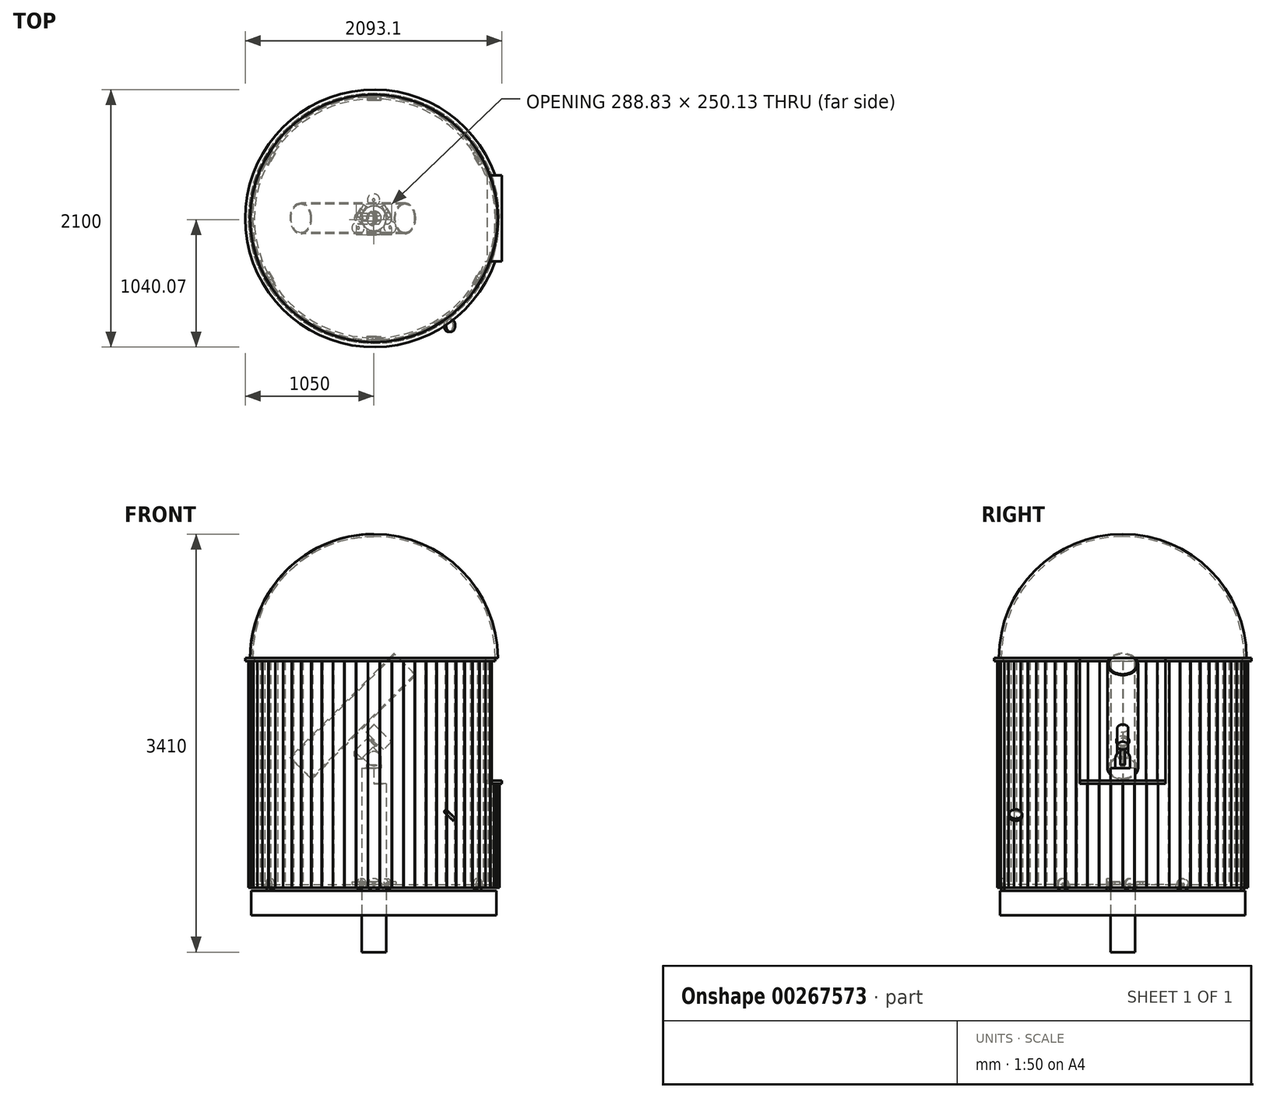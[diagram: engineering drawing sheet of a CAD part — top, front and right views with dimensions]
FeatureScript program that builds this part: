
annotation { "Feature Type Name" : "Feature", "Feature Type Description" : "" }
export const myFeature = defineFeature(function(context is Context, id is Id, definition is map)
    precondition{}
    {
        {
            assignVariable(context, id + "F0", {"name" : "Diameter", "anyValue" : 2000});
        }
        {
            assignVariable(context, id + "F1", {"name" : "Height", "anyValue" : 1850});
        }
        {
            assignVariable(context, id + "F2", {"name" : "TeleLength", "anyValue" : 1200});
        }
        {
            assignVariable(context, id + "F3", {"name" : "StandDia", "anyValue" : 200});
        }
        {
            var Q0;
            Q0=qCreatedBy(makeId("Top.planeOp"),FACE);
            var sketch = newSketch(context, id + "F4", { "sketchPlane" : qUnion([Q0])});
            skCircle(sketch, "E0", {"center": v(0, 0) * mm, "radius": 100 * mm});
            skSolve(sketch);
        }
        {
            var Q0;
            Q0 = qSketchRegion(id + "F4", true);
            extrude(context, id + "F5", {"entities" : qUnion([Q0]), "depth" : 1000 * mm, "hasSecondDirection" : true, "secondDirectionOppositeDirection" : true, "secondDirectionDepth" : 500 * mm});
        }
        {
            var Q0;
            Q0=qCreatedBy(makeId("Top.planeOp"),FACE);
            var sketch = newSketch(context, id + "F6", { "sketchPlane" : qUnion([Q0])});
            skCircle(sketch, "E1", {"center": v(0, 0) * mm, "radius": 1000 * mm});
            skSolve(sketch);
        }
        {
            var Q0;
            Q0 = qSketchRegion(id + "F6", true);
            extrude(context, id + "F7", {"entities" : qUnion([Q0]), "oppositeDirection" : true, "depth" : 200 * mm});
        }
        {
            var Q0;
            Q0=qCreatedBy(makeId("Front.planeOp"),FACE);
            cPlane(context, id + "F8", {"entities" : qUnion([Q0]), "cplaneType" : CPlaneType.OFFSET, "offset" : (getVariable(context, 'Diameter') / 2 - 10) * mm, "width" : 150 * mm, "height" : 150 * mm});
        }
        {
            var Q0;
            Q0=qCreatedBy(id+"F8.planeOp",FACE);
            var sketch = newSketch(context, id + "F9", { "sketchPlane" : qUnion([Q0])});
            skCircle(sketch, "E2", {"center": v(0, 50) * mm, "radius": 50 * mm});
            skCircle(sketch, "E3", {"center": v(0, 50) * mm, "radius": 10 * mm});
            skSolve(sketch);
        }
        {
            var Q0;
            Q0 = qSketchRegion(id + "F9", true);
            extrude(context, id + "F10", {"entities" : qUnion([Q0]), "oppositeDirection" : true, "depth" : 25 * mm});
        }
        {
            var Q0;
            Q0=makeQuery(id+"F10.opExtrude","SWEPT_BODY",BODY,{"disambiguationData":[OSD([sQuery(id+"F9.wireOp",EDGE,"E2"),sQuery(id+"F9.wireOp",EDGE,"E3")])]});
            var Q1;
            Q1=makeQuery(id+"F5.opExtrude","CAP_EDGE",EDGE,{"disambiguationData":[OSD([sQuery(id+"F4.wireOp",EDGE,"E0")])],"isStart":false});
            circularPattern(context, id + "F11", {"entities" : qUnion([Q0]), "axis" : qUnion([Q1]), "angle" : 360 * degree, "instanceCount" : 6, "equalSpace" : true});
        }
        {
            var Q0;
            Q0=makeQuery(id+"F10.opExtrude","SWEPT_BODY",BODY,{"disambiguationData":[OSD([sQuery(id+"F9.wireOp",EDGE,"E2"),sQuery(id+"F9.wireOp",EDGE,"E3")])]});
            transform(context, id + "F12", {"entities" : qUnion([Q0]), "transformType" : TransformType.TRANSLATION_3D, "dx" : 0 * mm, "dy" : (getVariable(context, 'Diameter') / 2 - getVariable(context, 'StandDia') / 2 - 40) * mm, "dz" : 0 * mm, "makeCopy" : true});
        }
        {
            var Q0;
            Q0=makeQuery(id+"F12.opPattern","COPY",BODY,{"derivedFrom":makeQuery(id+"F10.opExtrude","SWEPT_BODY",BODY,{"disambiguationData":[OSD([sQuery(id+"F9.wireOp",EDGE,"E2"),sQuery(id+"F9.wireOp",EDGE,"E3")])]}),"instanceName":"1"});
            var Q1;
            Q1=makeQuery(id+"F5.opExtrude","CAP_EDGE",EDGE,{"disambiguationData":[OSD([sQuery(id+"F4.wireOp",EDGE,"E0")])],"isStart":false});
            circularPattern(context, id + "F13", {"entities" : qUnion([Q0]), "axis" : qUnion([Q1]), "angle" : 360 * degree, "instanceCount" : 3, "equalSpace" : true});
        }
        {
            var Q0;
            Q0=makeQuery(id+"F7.opExtrude","CAP_FACE",FACE,{"disambiguationData":[OSD([sQuery(id+"F6.wireOp",EDGE,"E1")])],"isStart":true});
            cPlane(context, id + "F14", {"entities" : qUnion([Q0]), "cplaneType" : CPlaneType.OFFSET, "offset" : 25 * mm, "width" : 150 * mm, "height" : 150 * mm});
        }
        {
            var Q0;
            Q0=qCreatedBy(id+"F14.planeOp",FACE);
            var sketch = newSketch(context, id + "F15", { "sketchPlane" : qUnion([Q0])});
            skArc(sketch, "E4", {"start": v(55, -998.49) * mm, "mid": v(500, -866.03) * mm, "end": v(837.21, -546.87) * mm});
            skArc(sketch, "E5", {"start": v(52.92, -135) * mm, "mid": v(53.96, -134.59) * mm, "end": v(55, -134.16) * mm});
            skArc(sketch, "E6", {"start": v(55, -86.5) * mm, "mid": v(88.77, -51.25) * mm, "end": v(102.4, -4.38) * mm});
            skLineSegment(sketch, "E7", {"start": v(-55, -135) * mm, "end": v(55, -135) * mm});
            skLineSegment(sketch, "E8", {"start": v(-144.41, 19.87) * mm, "end": v(-89.41, 115.13) * mm});
            skLineSegment(sketch, "E9", {"start": v(144.41, 19.87) * mm, "end": v(89.41, 115.13) * mm});
            skLineSegment(sketch, "E10", {"start": v(55, -135) * mm, "end": v(55, -86.5) * mm});
            skLineSegment(sketch, "E11", {"start": v(-55, -135) * mm, "end": v(-55, -86.5) * mm});
            skLineSegment(sketch, "E12", {"start": v(-144.41, 19.87) * mm, "end": v(-102.4, -4.38) * mm});
            skLineSegment(sketch, "E13", {"start": v(-89.41, 115.13) * mm, "end": v(-47.4, 90.88) * mm});
            skLineSegment(sketch, "E14", {"start": v(102.4, -4.38) * mm, "end": v(144.41, 19.87) * mm});
            skLineSegment(sketch, "E15", {"start": v(47.4, 90.88) * mm, "end": v(89.41, 115.13) * mm});
            skLineSegment(sketch, "E16", {"start": v(-50, -130) * mm, "end": v(-50, -105) * mm, "construction": true});
            skLineSegment(sketch, "E17", {"start": v(50, -105) * mm, "end": v(50, -130) * mm, "construction": true});
            skLineSegment(sketch, "E18", {"start": v(137.58, 21.7) * mm, "end": v(115.93, 9.2) * mm, "construction": true});
            skLineSegment(sketch, "E19", {"start": v(65.93, 95.8) * mm, "end": v(87.58, 108.3) * mm, "construction": true});
            skLineSegment(sketch, "E20", {"start": v(-87.58, 108.3) * mm, "end": v(-65.93, 95.8) * mm, "construction": true});
            skLineSegment(sketch, "E21", {"start": v(-115.93, 9.2) * mm, "end": v(-137.58, 21.7) * mm, "construction": true});
            skPoint(sketch, "E22.orphan", {"position": v(159.25, -135) * mm});
            skArc(sketch, "E23.trimOffspring", {"start": v(143.69, 19.45) * mm, "mid": v(143.53, 20.56) * mm, "end": v(143.37, 21.67) * mm});
            skArc(sketch, "E24.trimOffspring", {"start": v(90.46, 113.33) * mm, "mid": v(89.58, 114.02) * mm, "end": v(88.69, 114.71) * mm});
            skPoint(sketch, "E25.orphan", {"position": v(159.25, 155.45) * mm});
            skArc(sketch, "E26.trimOffspring", {"start": v(-88.69, 114.71) * mm, "mid": v(-89.58, 114.02) * mm, "end": v(-90.46, 113.33) * mm});
            skArc(sketch, "E27.trimOffspring", {"start": v(47.4, 90.88) * mm, "mid": v(0, 102.5) * mm, "end": v(-47.4, 90.88) * mm});
            skArc(sketch, "E28.trimOffspring", {"start": v(-102.4, -4.38) * mm, "mid": v(-88.77, -51.25) * mm, "end": v(-55, -86.5) * mm});
            skArc(sketch, "E29.trimOffspring", {"start": v(-143.37, 21.67) * mm, "mid": v(-143.53, 20.56) * mm, "end": v(-143.69, 19.45) * mm});
            skArc(sketch, "E30.trimOffspring", {"start": v(-55, -134.16) * mm, "mid": v(-53.96, -134.59) * mm, "end": v(-52.92, -135) * mm});
            skLineSegment(sketch, "E31", {"start": v(-55, -998.49) * mm, "end": v(-55, -960) * mm});
            skLineSegment(sketch, "E32", {"start": v(-55, -960) * mm, "end": v(55, -960) * mm});
            skLineSegment(sketch, "E33", {"start": v(55, -998.49) * mm, "end": v(55, -960) * mm});
            skLineSegment(sketch, "E34", {"start": v(-50, -990) * mm, "end": v(-50, -965) * mm, "construction": true});
            skLineSegment(sketch, "E35", {"start": v(50, -965) * mm, "end": v(50, -990) * mm, "construction": true});
            skLineSegment(sketch, "E36.1.0", {"start": v(860.71, -439.2) * mm, "end": v(882.37, -451.7) * mm, "construction": true});
            skLineSegment(sketch, "E36.1.1", {"start": v(803.88, -527.63) * mm, "end": v(858.88, -432.37) * mm});
            skLineSegment(sketch, "E36.1.2", {"start": v(832.37, -538.3) * mm, "end": v(810.71, -525.8) * mm, "construction": true});
            skLineSegment(sketch, "E36.1.3", {"start": v(837.21, -546.87) * mm, "end": v(803.88, -527.63) * mm});
            skLineSegment(sketch, "E36.1.4", {"start": v(892.21, -451.61) * mm, "end": v(858.88, -432.37) * mm});
            skLineSegment(sketch, "E36.2.0", {"start": v(810.71, 525.8) * mm, "end": v(832.37, 538.3) * mm, "construction": true});
            skLineSegment(sketch, "E36.2.1", {"start": v(858.88, 432.37) * mm, "end": v(803.88, 527.63) * mm});
            skLineSegment(sketch, "E36.2.2", {"start": v(882.37, 451.7) * mm, "end": v(860.71, 439.2) * mm, "construction": true});
            skLineSegment(sketch, "E36.2.3", {"start": v(892.21, 451.61) * mm, "end": v(858.88, 432.37) * mm});
            skLineSegment(sketch, "E36.2.4", {"start": v(837.21, 546.87) * mm, "end": v(803.88, 527.63) * mm});
            skLineSegment(sketch, "E36.3.0", {"start": v(-50, 965) * mm, "end": v(-50, 990) * mm, "construction": true});
            skLineSegment(sketch, "E36.3.1", {"start": v(55, 960) * mm, "end": v(-55, 960) * mm});
            skLineSegment(sketch, "E36.3.2", {"start": v(50, 990) * mm, "end": v(50, 965) * mm, "construction": true});
            skLineSegment(sketch, "E36.3.3", {"start": v(55, 998.49) * mm, "end": v(55, 960) * mm});
            skLineSegment(sketch, "E36.3.4", {"start": v(-55, 998.49) * mm, "end": v(-55, 960) * mm});
            skLineSegment(sketch, "E36.4.0", {"start": v(-860.71, 439.2) * mm, "end": v(-882.37, 451.7) * mm, "construction": true});
            skLineSegment(sketch, "E36.4.1", {"start": v(-803.88, 527.63) * mm, "end": v(-858.88, 432.37) * mm});
            skLineSegment(sketch, "E36.4.2", {"start": v(-832.37, 538.3) * mm, "end": v(-810.71, 525.8) * mm, "construction": true});
            skLineSegment(sketch, "E36.4.3", {"start": v(-837.21, 546.87) * mm, "end": v(-803.88, 527.63) * mm});
            skLineSegment(sketch, "E36.4.4", {"start": v(-892.21, 451.61) * mm, "end": v(-858.88, 432.37) * mm});
            skLineSegment(sketch, "E36.5.0", {"start": v(-810.71, -525.8) * mm, "end": v(-832.37, -538.3) * mm, "construction": true});
            skLineSegment(sketch, "E36.5.1", {"start": v(-858.88, -432.37) * mm, "end": v(-803.88, -527.63) * mm});
            skLineSegment(sketch, "E36.5.2", {"start": v(-882.37, -451.7) * mm, "end": v(-860.71, -439.2) * mm, "construction": true});
            skLineSegment(sketch, "E36.5.3", {"start": v(-892.21, -451.61) * mm, "end": v(-858.88, -432.37) * mm});
            skLineSegment(sketch, "E36.5.4", {"start": v(-837.21, -546.87) * mm, "end": v(-803.88, -527.63) * mm});
            skArc(sketch, "E37.trimOffspring", {"start": v(-837.21, -546.87) * mm, "mid": v(-500, -866.03) * mm, "end": v(-55, -998.49) * mm});
            skArc(sketch, "E38.trimOffspring", {"start": v(-892.21, 451.61) * mm, "mid": v(-1000, 0) * mm, "end": v(-892.21, -451.61) * mm});
            skArc(sketch, "E39.trimOffspring", {"start": v(-55, 998.49) * mm, "mid": v(-500, 866.03) * mm, "end": v(-837.21, 546.87) * mm});
            skArc(sketch, "E40.trimOffspring", {"start": v(837.21, 546.87) * mm, "mid": v(500, 866.03) * mm, "end": v(55, 998.49) * mm});
            skArc(sketch, "E41.trimOffspring", {"start": v(892.21, -451.61) * mm, "mid": v(1000, 0) * mm, "end": v(892.21, 451.61) * mm});
            skSolve(sketch);
        }
        {
            var Q0;
            Q0 = qSketchRegion(id + "F15", true);
            extrude(context, id + "F16", {"entities" : qUnion([Q0]), "depth" : 25 * mm});
        }
        {
            var Q0;
            Q0=makeQuery(id+"F16.opExtrude","CAP_FACE",FACE,{"disambiguationData":[OSD([sQuery(id+"F15.wireOp",EDGE,"E4"),sQuery(id+"F15.wireOp",EDGE,"E6"),sQuery(id+"F15.wireOp",EDGE,"E7"),sQuery(id+"F15.wireOp",EDGE,"E8"),sQuery(id+"F15.wireOp",EDGE,"E9"),sQuery(id+"F15.wireOp",EDGE,"E10"),sQuery(id+"F15.wireOp",EDGE,"E11"),sQuery(id+"F15.wireOp",EDGE,"E12"),sQuery(id+"F15.wireOp",EDGE,"E13"),sQuery(id+"F15.wireOp",EDGE,"E14"),sQuery(id+"F15.wireOp",EDGE,"E15"),sQuery(id+"F15.wireOp",EDGE,"E27.trimOffspring"),sQuery(id+"F15.wireOp",EDGE,"E28.trimOffspring")])],"isStart":false});
            var sketch = newSketch(context, id + "F17", { "sketchPlane" : qUnion([Q0])});
            skCircle(sketch, "E42", {"center": v(131.23, -72.66) * mm, "radius": 50 * mm});
            skLineSegment(sketch, "E43", {"start": v(0, 0) * mm, "end": v(285.88, -158.3) * mm, "construction": true});
            skLineSegment(sketch, "E44", {"start": v(0, 0) * mm, "end": v(432.41, 7.74) * mm, "construction": true});
            skPoint(sketch, "E44.endSnap0", {"position": v(123.4, 7.74) * mm});
            skCircle(sketch, "E45", {"center": v(131.23, -72.66) * mm, "radius": 10 * mm});
            skSolve(sketch);
        }
        {
            var Q0;
            Q0 = qSketchRegion(id + "F17", true);
            extrude(context, id + "F18", {"entities" : qUnion([Q0]), "depth" : 25 * mm});
        }
        {
            var Q0;
            Q0=makeQuery(id+"F18.opExtrude","SWEPT_BODY",BODY,{"disambiguationData":[OSD([sQuery(id+"F17.wireOp",EDGE,"E42"),sQuery(id+"F17.wireOp",EDGE,"E45")])]});
            var Q1;
            Q1=makeQuery(id+"F5.opExtrude","CAP_EDGE",EDGE,{"disambiguationData":[OSD([sQuery(id+"F4.wireOp",EDGE,"E0")])],"isStart":false});
            circularPattern(context, id + "F19", {"entities" : qUnion([Q0]), "axis" : qUnion([Q1]), "angle" : 360 * degree, "instanceCount" : 3, "equalSpace" : true});
        }
        {
            var Q0;
            Q0=qCreatedBy(id+"F14.planeOp",FACE);
            var sketch = newSketch(context, id + "F20", { "sketchPlane" : qUnion([Q0])});
            skLineSegment(sketch, "E46.bottom", {"start": v(47.5, -1022) * mm, "end": v(-47.5, -1022) * mm});
            skLineSegment(sketch, "E46.top", {"start": v(47.5, -1000) * mm, "end": v(-47.5, -1000) * mm});
            skLineSegment(sketch, "E46.left", {"start": v(47.5, -1022) * mm, "end": v(47.5, -1000) * mm});
            skLineSegment(sketch, "E46.right", {"start": v(-47.5, -1022) * mm, "end": v(-47.5, -1000) * mm});
            skPoint(sketch, "E46.middle", {"position": v(0, -1011) * mm});
            skSolve(sketch);
        }
        {
            var Q0;
            Q0 = qSketchRegion(id + "F20", true);
            extrude(context, id + "F21", {"entities" : qUnion([Q0]), "depth" : (getVariable(context, 'Height')) * mm});
        }
        {
            var Q0;
            Q0=makeQuery(id+"F21.opExtrude","SWEPT_BODY",BODY,{"disambiguationData":[OSD([sQuery(id+"F20.wireOp",EDGE,"E46.bottom"),sQuery(id+"F20.wireOp",EDGE,"E46.top"),sQuery(id+"F20.wireOp",EDGE,"E46.left"),sQuery(id+"F20.wireOp",EDGE,"E46.right")])]});
            var Q1;
            Q1=makeQuery(id+"F5.opExtrude","CAP_EDGE",EDGE,{"disambiguationData":[OSD([sQuery(id+"F4.wireOp",EDGE,"E0")])],"isStart":false});
            circularPattern(context, id + "F22", {"entities" : qUnion([Q0]), "axis" : qUnion([Q1]), "angle" : 360 * degree, "instanceCount" : floor(getVariable(context, 'Diameter') * PI / 95), "equalSpace" : true});
        }
        {
            var Q0;
            Q0=qCreatedBy(makeId("Right.planeOp"),FACE);
            var sketch = newSketch(context, id + "F23", { "sketchPlane" : qUnion([Q0])});
            skLineSegment(sketch, "E47.bottom", {"start": v(350, 875) * mm, "end": v(-350, 875) * mm});
            skLineSegment(sketch, "E47.top", {"start": v(350, 2256.82) * mm, "end": v(-350, 2256.82) * mm});
            skLineSegment(sketch, "E47.left", {"start": v(350, 875) * mm, "end": v(350, 2256.82) * mm});
            skLineSegment(sketch, "E47.right", {"start": v(-350, 875) * mm, "end": v(-350, 2256.82) * mm});
            skPoint(sketch, "E47.middle", {"position": v(0, 1565.9) * mm});
            skSolve(sketch);
        }
        {
            var Q0;
            Q0 = qSketchRegion(id + "F23", true);
            extrude(context, id + "F24", {"entities" : qUnion([Q0]), "operationType" : NewBodyOperationType.REMOVE, "endBound" : BoundingType.THROUGH_ALL, "depth" : 25 * mm});
        }
        {
            var Q0;
            Q0=makeQuery(id+"F5.opExtrude","CAP_FACE",FACE,{"disambiguationData":[OSD([sQuery(id+"F4.wireOp",EDGE,"E0")])],"isStart":false});
            var sketch = newSketch(context, id + "F25", { "sketchPlane" : qUnion([Q0])});
            skCircle(sketch, "E48", {"center": v(0, 0) * mm, "radius": 60 * mm});
            skSolve(sketch);
        }
        {
            var Q0;
            Q0 = qSketchRegion(id + "F25", true);
            extrude(context, id + "F26", {"entities" : qUnion([Q0]), "depth" : 50 * mm});
        }
        {
            var Q0;
            Q0=qCreatedBy(makeId("Right.planeOp"),FACE);
            var sketch = newSketch(context, id + "F27", { "sketchPlane" : qUnion([Q0])});
            skLineSegment(sketch, "E49.0", {"start": v(-60, 1050) * mm, "end": v(60, 1050) * mm, "construction": true});
            skLineSegment(sketch, "E50", {"start": v(-60, 1050) * mm, "end": v(-60, 1080) * mm});
            skLineSegment(sketch, "E51", {"start": v(0, 1050) * mm, "end": v(0, 1140) * mm});
            skPoint(sketch, "E51.endSnap0", {"position": v(0, 1050) * mm});
            skLineSegment(sketch, "E52", {"start": v(0, 1050) * mm, "end": v(-60, 1050) * mm});
            skArc(sketch, "E53", {"start": v(-60, 1080) * mm, "mid": v(-42.43, 1122.43) * mm, "end": v(0, 1140) * mm});
            skSolve(sketch);
        }
        {
            var Q0;
            Q0 = qSketchRegion(id + "F27", true);
            var Q1;
            Q1=makeQuery(id+"F26.opExtrude","CAP_EDGE",EDGE,{"disambiguationData":[OSD([sQuery(id+"F25.wireOp",EDGE,"E48")])],"isStart":false});
            revolve(context, id + "F28", {"operationType" : NewBodyOperationType.ADD, "entities" : qUnion([Q0]), "axis" : qUnion([Q1]), "revolveType" : RevolveType.FULL});
        }
        {
            var Q0;
            Q0=qCreatedBy(makeId("Right.planeOp"),FACE);
            var sketch = newSketch(context, id + "F29", { "sketchPlane" : qUnion([Q0])});
            skLineSegment(sketch, "E54.bottom", {"start": v(20, 1030) * mm, "end": v(-20, 1030) * mm});
            skLineSegment(sketch, "E54.top", {"start": v(20, 1302) * mm, "end": v(-20, 1302) * mm});
            skLineSegment(sketch, "E54.left", {"start": v(20, 1030) * mm, "end": v(20, 1302) * mm});
            skLineSegment(sketch, "E54.right", {"start": v(-20, 1030) * mm, "end": v(-20, 1302) * mm});
            skPoint(sketch, "E54.middle", {"position": v(0, 1166) * mm});
            skSolve(sketch);
        }
        {
            var Q0;
            Q0 = qSketchRegion(id + "F29", true);
            extrude(context, id + "F30", {"entities" : qUnion([Q0]), "operationType" : NewBodyOperationType.REMOVE, "endBound" : BoundingType.SYMMETRIC, "oppositeDirection" : true, "depth" : 158 * mm});
        }
        {
            var Q0;
            Q0=qCreatedBy(makeId("Front.planeOp"),FACE);
            var sketch = newSketch(context, id + "F31", { "sketchPlane" : qUnion([Q0])});
            skLineSegment(sketch, "E55", {"start": v(-91.92, 1087.07) * mm, "end": v(-7.07, 1171.92) * mm});
            skLineSegment(sketch, "E56", {"start": v(-7.07, 1171.92) * mm, "end": v(42.43, 1122.43) * mm});
            skLineSegment(sketch, "E57", {"start": v(-91.92, 1087.07) * mm, "end": v(-42.43, 1037.57) * mm});
            skArc(sketch, "E58.0", {"start": v(56.57, 1080) * mm, "mid": v(0, 1136.57) * mm, "end": v(-56.57, 1080) * mm, "construction": true});
            skLineSegment(sketch, "E59", {"start": v(-42.43, 1037.57) * mm, "end": v(42.43, 1122.43) * mm, "construction": true});
            skArc(sketch, "E60", {"start": v(42.43, 1122.43) * mm, "mid": v(42.43, 1037.57) * mm, "end": v(-42.43, 1037.57) * mm});
            skLineSegment(sketch, "E61", {"start": v(0, 1080) * mm, "end": v(0, 1289.36) * mm, "construction": true});
            skSolve(sketch);
        }
        {
            var Q0;
            Q0 = qSketchRegion(id + "F31", true);
            extrude(context, id + "F32", {"entities" : qUnion([Q0]), "endBound" : BoundingType.SYMMETRIC, "depth" : 40 * mm});
        }
        {
            var Q0;
            Q0=makeQuery(id+"F32.opExtrude","SWEPT_FACE",FACE,{"disambiguationData":[OSD([sQuery(id+"F31.wireOp",EDGE,"E55")])]});
            cPlane(context, id + "F33", {"entities" : qUnion([Q0]), "cplaneType" : CPlaneType.OFFSET, "offset" : 25 * mm, "width" : 150 * mm, "height" : 150 * mm});
        }
        {
            var Q0;
            Q0=qCreatedBy(makeId("Front.planeOp"),FACE);
            var sketch = newSketch(context, id + "F34", { "sketchPlane" : qUnion([Q0])});
            skLineSegment(sketch, "E62", {"start": v(-9.1, 1225.9) * mm, "end": v(-148.05, 1086.96) * mm});
            skLineSegment(sketch, "E63", {"start": v(-148.05, 1086.96) * mm, "end": v(-136.78, 1075.7) * mm});
            skLineSegment(sketch, "E64", {"start": v(-136.78, 1075.7) * mm, "end": v(-96.42, 1075.5) * mm});
            skLineSegment(sketch, "E65", {"start": v(-96.42, 1075.5) * mm, "end": v(9.63, 1181.55) * mm});
            skLineSegment(sketch, "E66", {"start": v(9.63, 1181.55) * mm, "end": v(20.43, 1180.8) * mm});
            skLineSegment(sketch, "E67", {"start": v(20.43, 1180.8) * mm, "end": v(28.21, 1188.59) * mm});
            skLineSegment(sketch, "E68", {"start": v(28.21, 1188.59) * mm, "end": v(-9.1, 1225.9) * mm});
            skSolve(sketch);
        }
        {
            var Q0;
            Q0 = qSketchRegion(id + "F34", true);
            var Q1;
            Q1=sQuery(id+"F34.wireOp",EDGE,"E62");
            revolve(context, id + "F35", {"operationType" : NewBodyOperationType.ADD, "entities" : qUnion([Q0]), "axis" : qUnion([Q1]), "revolveType" : RevolveType.FULL});
        }
        {
            var Q0;
            Q0=makeQuery(id+"F35.opRevolve","SWEPT_FACE",FACE,{"disambiguationData":[OSD([sQuery(id+"F34.wireOp",EDGE,"E68")])]});
            cPlane(context, id + "F36", {"entities" : qUnion([Q0]), "cplaneType" : CPlaneType.OFFSET, "offset" : 25 * mm, "width" : 150 * mm, "height" : 150 * mm});
        }
        {
            var Q0;
            Q0=makeQuery(id+"F35.opRevolve","SWEPT_FACE",FACE,{"disambiguationData":[OSD([sQuery(id+"F34.wireOp",EDGE,"E68")])]});
            var sketch = newSketch(context, id + "F37", { "sketchPlane" : qUnion([Q0])});
            skCircle(sketch, "E69.0", {"center": v(-873.28, 0) * mm, "radius": 52.78 * mm});
            skSolve(sketch);
        }
        {
            var Q0;
            Q0 = qSketchRegion(id + "F37", true);
            extrude(context, id + "F38", {"entities" : qUnion([Q0]), "depth" : 25 * mm});
        }
        {
            var Q0;
            Q0=qCreatedBy(id+"F33.planeOp",FACE);
            var sketch = newSketch(context, id + "F39", { "sketchPlane" : qUnion([Q0])});
            skCircle(sketch, "E70", {"center": v(0, 915.4) * mm, "radius": 45 * mm});
            skSolve(sketch);
        }
        {
            var Q0;
            Q0 = qSketchRegion(id + "F39", true);
            extrude(context, id + "F40", {"entities" : qUnion([Q0]), "operationType" : NewBodyOperationType.ADD, "endBound" : BoundingType.SYMMETRIC, "depth" : 200 * mm});
        }
        {
            var Q0;
            Q0=qCreatedBy(id+"F36.planeOp",FACE);
            var sketch = newSketch(context, id + "F41", { "sketchPlane" : qUnion([Q0])});
            skCircle(sketch, "E71", {"center": v(0, 1128.68) * mm, "radius": 125 * mm});
            skCircle(sketch, "E72", {"center": v(0, 1128.68) * mm, "radius": 115 * mm});
            skSolve(sketch);
        }
        {
            var Q0;
            Q0 = qSketchRegion(id + "F41", true);
            extrude(context, id + "F42", {"entities" : qUnion([Q0]), "endBound" : BoundingType.SYMMETRIC, "depth" : (getVariable(context, 'TeleLength')) * mm});
        }
        {
            var Q0;
            Q0=makeQuery(id+"F24.boolean.opBoolean","COPY",FACE,{"disambiguationData":[TD([makeQuery(id+"F22.opPattern","COPY",FACE,{"derivedFrom":makeQuery(id+"F21.opExtrude","SWEPT_FACE",FACE,{"disambiguationData":[OSD([sQuery(id+"F20.wireOp",EDGE,"E46.bottom")])]}),"instanceName":"14"})])],"derivedFrom":makeQuery(id+"F24.opExtrude","SWEPT_FACE",FACE,{"disambiguationData":[OSD([sQuery(id+"F23.wireOp",EDGE,"E47.bottom")])]})});
            var sketch = newSketch(context, id + "F43", { "sketchPlane" : qUnion([Q0])});
            skLineSegment(sketch, "E73.bottom", {"start": v(1043.1, 350) * mm, "end": v(923.1, 350) * mm});
            skLineSegment(sketch, "E73.top", {"start": v(1043.1, -350) * mm, "end": v(923.1, -350) * mm});
            skLineSegment(sketch, "E73.left", {"start": v(1043.1, 350) * mm, "end": v(1043.1, -350) * mm});
            skLineSegment(sketch, "E73.right", {"start": v(923.1, 350) * mm, "end": v(923.1, -350) * mm});
            skPoint(sketch, "E73.middle", {"position": v(983.1, 0) * mm});
            skSolve(sketch);
        }
        {
            var Q0;
            Q0 = qSketchRegion(id + "F43", true);
            extrude(context, id + "F44", {"entities" : qUnion([Q0]), "depth" : 25 * mm});
        }
        {
            var Q0;
            Q0=makeQuery(id+"F22.opPattern","COPY",FACE,{"derivedFrom":makeQuery(id+"F21.opExtrude","CAP_FACE",FACE,{"disambiguationData":[OSD([sQuery(id+"F20.wireOp",EDGE,"E46.bottom"),sQuery(id+"F20.wireOp",EDGE,"E46.top"),sQuery(id+"F20.wireOp",EDGE,"E46.left"),sQuery(id+"F20.wireOp",EDGE,"E46.right")])],"isStart":false}),"instanceName":"10"});
            var sketch = newSketch(context, id + "F45", { "sketchPlane" : qUnion([Q0])});
            skArc(sketch, "E74", {"start": v(989.95, 350) * mm, "mid": v(-1050, 0) * mm, "end": v(989.95, -350) * mm});
            skArc(sketch, "E75", {"start": v(910.01, 350) * mm, "mid": v(-975, 0) * mm, "end": v(910.01, -350) * mm});
            skLineSegment(sketch, "E76", {"start": v(774.53, -350) * mm, "end": v(1167.33, -350) * mm, "construction": true});
            skLineSegment(sketch, "E77", {"start": v(753, 350) * mm, "end": v(1167.33, 350) * mm, "construction": true});
            skLineSegment(sketch, "E78", {"start": v(910.01, -350) * mm, "end": v(910.01, 350) * mm, "construction": true});
            skLineSegment(sketch, "E79", {"start": v(989.95, -350) * mm, "end": v(989.95, 350) * mm, "construction": true});
            skLineSegment(sketch, "E80", {"start": v(910.01, -350) * mm, "end": v(989.95, -350) * mm});
            skLineSegment(sketch, "E81", {"start": v(910.01, 350) * mm, "end": v(989.95, 350) * mm});
            skSolve(sketch);
        }
        {
            var Q0;
            Q0 = qSketchRegion(id + "F45", true);
            extrude(context, id + "F46", {"entities" : qUnion([Q0]), "depth" : 25 * mm});
        }
        {
            var Q0;
            Q0=qCreatedBy(makeId("Front.planeOp"),FACE);
            var sketch = newSketch(context, id + "F47", { "sketchPlane" : qUnion([Q0])});
            skArc(sketch, "E82", {"start": v(-990, 1900) * mm, "mid": v(-700.04, 2600.04) * mm, "end": v(0, 2890) * mm});
            skArc(sketch, "E83", {"start": v(-1010, 1900) * mm, "mid": v(-714.18, 2614.18) * mm, "end": v(0, 2910) * mm});
            skLineSegment(sketch, "E84", {"start": v(0, 2890) * mm, "end": v(0, 2910) * mm});
            skLineSegment(sketch, "E85", {"start": v(-990, 1900) * mm, "end": v(-1010, 1900) * mm});
            skSolve(sketch);
        }
        {
            var Q0;
            Q0 = qSketchRegion(id + "F47", true);
            var Q1;
            Q1=makeQuery(id+"F46.opExtrude","SWEPT_FACE",FACE,{"disambiguationData":[OSD([sQuery(id+"F45.wireOp",EDGE,"E74")])]});
            revolve(context, id + "F48", {"entities" : qUnion([Q0]), "axis" : qUnion([Q1]), "revolveType" : RevolveType.FULL});
        }
    });
